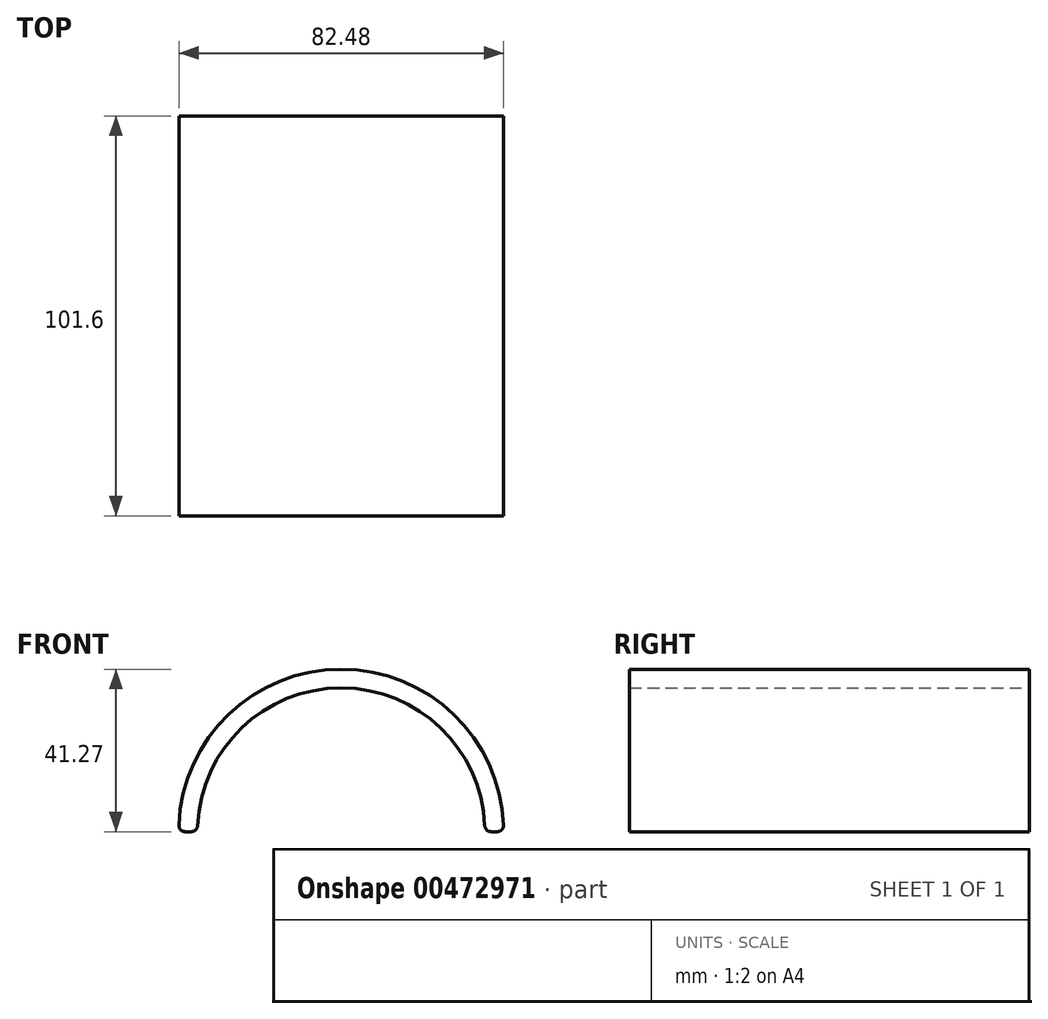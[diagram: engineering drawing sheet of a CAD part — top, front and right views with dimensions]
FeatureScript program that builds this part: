
annotation { "Feature Type Name" : "Feature", "Feature Type Description" : "" }
export const myFeature = defineFeature(function(context is Context, id is Id, definition is map)
    precondition{}
    {
        {
            var Q0;
            Q0=qCreatedBy(makeId("Front.planeOp"),FACE);
            var sketch = newSketch(context, id + "F0", { "sketchPlane" : qUnion([Q0])});
            skArc(sketch, "E0", {"start": v(36.51, 0) * mm, "mid": v(0, 36.51) * mm, "end": v(-36.51, 0) * mm});
            skArc(sketch, "E1", {"start": v(41.28, 0) * mm, "mid": v(0, 41.28) * mm, "end": v(-41.28, 0) * mm});
            skLineSegment(sketch, "E2", {"start": v(-41.28, 0) * mm, "end": v(-36.51, 0) * mm});
            skLineSegment(sketch, "E3.trimOffspring", {"start": v(36.51, 0) * mm, "end": v(41.28, 0) * mm});
            skSolve(sketch);
        }
        {
            var Q0;
            Q0 = qSketchRegion(id + "F0", true);
            extrude(context, id + "F1", {"entities" : qUnion([Q0]), "endBound" : BoundingType.SYMMETRIC, "depth" : 101.6 * mm});
        }
        {
            var Q0;
            Q0=makeQuery(id+"F1.opExtrude","SWEPT_EDGE",EDGE,{"disambiguationData":[OSD([sQuery(id+"F0.wireOp",EDGE,"E1"),sQuery(id+"F0.wireOp",EDGE,"E2")])]});
            var Q1;
            Q1=makeQuery(id+"F1.opExtrude","SWEPT_EDGE",EDGE,{"disambiguationData":[OSD([sQuery(id+"F0.wireOp",EDGE,"E0"),sQuery(id+"F0.wireOp",EDGE,"E2")])]});
            var Q2;
            Q2=makeQuery(id+"F1.opExtrude","SWEPT_EDGE",EDGE,{"disambiguationData":[OSD([sQuery(id+"F0.wireOp",EDGE,"E0"),sQuery(id+"F0.wireOp",EDGE,"E3.trimOffspring")])]});
            var Q3;
            Q3=makeQuery(id+"F1.opExtrude","SWEPT_EDGE",EDGE,{"disambiguationData":[OSD([sQuery(id+"F0.wireOp",EDGE,"E1"),sQuery(id+"F0.wireOp",EDGE,"E3.trimOffspring")])]});
            fillet(context, id + "F2", {"entities" : qUnion([Q0, Q1, Q2, Q3]), "radius" : 1.59 * mm, "tangentPropagation" : true, "allowEdgeOverflow" : false});
        }
    });
